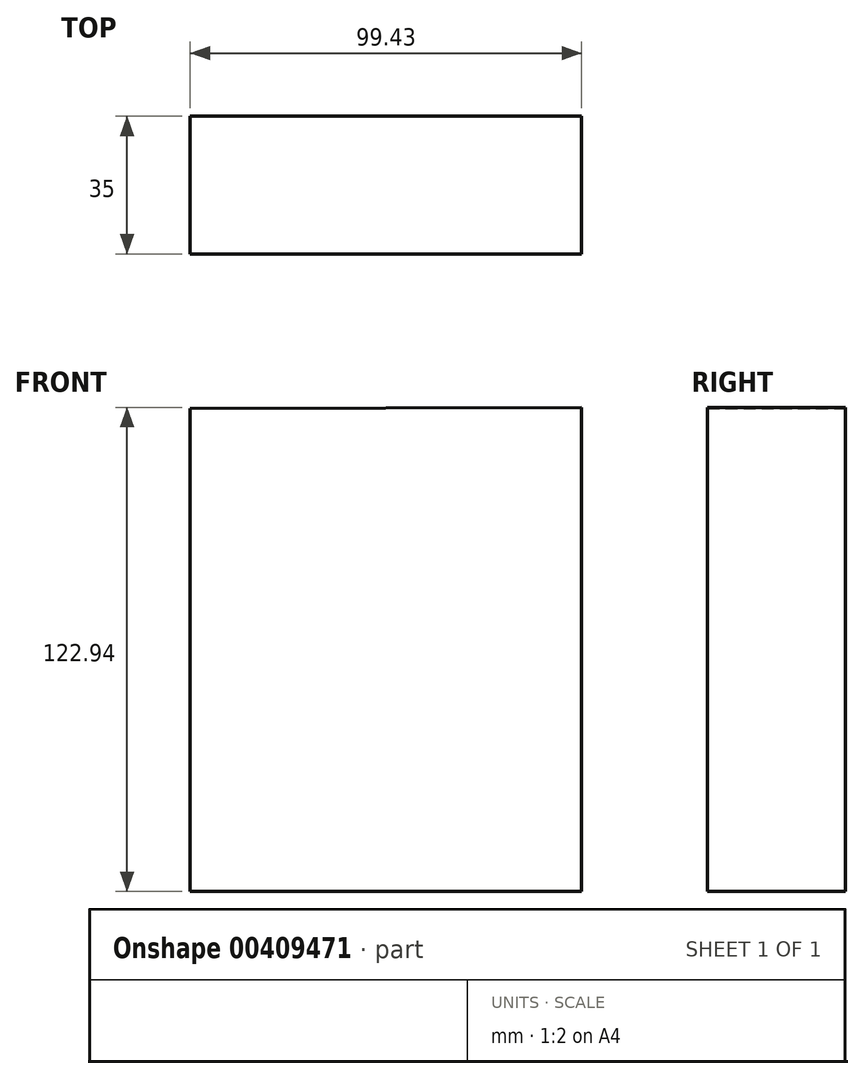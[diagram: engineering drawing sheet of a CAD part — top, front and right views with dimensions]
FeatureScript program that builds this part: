
annotation { "Feature Type Name" : "Feature", "Feature Type Description" : "" }
export const myFeature = defineFeature(function(context is Context, id is Id, definition is map)
    precondition{}
    {
        {
            var Q0;
            Q0=qCreatedBy(makeId("Front.planeOp"),FACE);
            var sketch = newSketch(context, id + "F0", { "sketchPlane" : qUnion([Q0])});
            skLineSegment(sketch, "E0", {"start": v(-56.37, 60.05) * mm, "end": v(-56.37, -62.6) * mm});
            skLineSegment(sketch, "E1", {"start": v(-56.37, -62.6) * mm, "end": v(43.06, -62.6) * mm});
            skLineSegment(sketch, "E2", {"start": v(43.06, -62.6) * mm, "end": v(43.06, 60.34) * mm});
            skLineSegment(sketch, "E3", {"start": v(43.06, 60.34) * mm, "end": v(-56.37, 60.05) * mm});
            skSolve(sketch);
        }
        {
            var Q0;
            Q0=makeQuery(id+"F0.imprint","IMPRINT",FACE,{"disambiguationData":[TD([[makeQuery(id+"F0.imprint","IMPRINT",EDGE,{"derivedFrom":sQuery(id+"F0.wireOp",EDGE,"E0")}),1.0]])]});
            extrude(context, id + "F1", {"entities" : qUnion([Q0]), "depth" : 10 * mm});
        }
        {
            var Q0;
            Q0=qCreatedBy(makeId("Right.planeOp"),FACE);
            var sketch = newSketch(context, id + "F2", { "sketchPlane" : qUnion([Q0])});
            skLineSegment(sketch, "E4", {"start": v(-9.91, -62.6) * mm, "end": v(-72.52, -62.6) * mm});
            skLineSegment(sketch, "E5", {"start": v(-72.52, -62.6) * mm, "end": v(-72.52, 38.24) * mm});
            skLineSegment(sketch, "E6", {"start": v(-72.52, 38.24) * mm, "end": v(-66.57, 38.24) * mm});
            skLineSegment(sketch, "E7", {"start": v(-66.57, 38.24) * mm, "end": v(-66.57, -54.39) * mm});
            skLineSegment(sketch, "E8", {"start": v(-66.57, -54.39) * mm, "end": v(-10.2, -54.39) * mm});
            skSolve(sketch);
        }
        {
            var Q0;
            Q0 = qSketchRegion(id + "F2", true);
            var Q1;
            Q1=makeQuery(id+"F1.opExtrude","CAP_FACE",FACE,{"disambiguationData":[OSD([sQuery(id+"F0.wireOp",EDGE,"E0"),sQuery(id+"F0.wireOp",EDGE,"E1"),sQuery(id+"F0.wireOp",EDGE,"E2"),sQuery(id+"F0.wireOp",EDGE,"E3")])],"isStart":false});
            var Q2;
            Q2=makeQuery(id+"F1.opExtrude","CAP_FACE",FACE,{"disambiguationData":[OSD([sQuery(id+"F0.wireOp",EDGE,"E0"),sQuery(id+"F0.wireOp",EDGE,"E1"),sQuery(id+"F0.wireOp",EDGE,"E2"),sQuery(id+"F0.wireOp",EDGE,"E3")])],"isStart":true});
            extrude(context, id + "F3", {"entities" : qUnion([Q0, Q1, Q2]), "operationType" : NewBodyOperationType.ADD, "depth" : 25 * mm});
        }
    });
